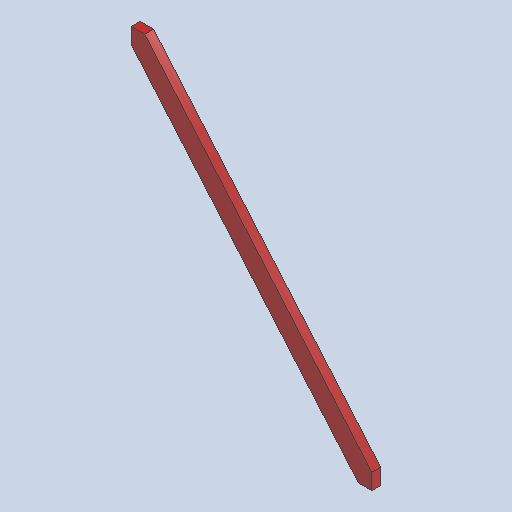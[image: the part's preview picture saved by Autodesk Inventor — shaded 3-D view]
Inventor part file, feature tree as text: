
AUTODESK INVENTOR PART (.ipt)
format: ipt  version: 2025 (Build 290162000, 162)  size: 95,744 bytes
history: native  units: in
note: dims shown in document units (in); Inventor stores cm internally (conversion verified against a paired STEP export)
features: other x4, sketch x1
ambient origin geometry x8: Origin, YZ Plane, XZ Plane, XY Plane, X Axis, Y Axis, Z Axis, Center Point
bodies: Solid1 (feature_tree)
feature tree (5):
  other  "44x2x4_MIR.ipt"
  other  "Solid1::44x2x4_MIR.ipt"
  other  "TaggingFeature1"
  sketch  "Sketch1"  dims[d0=0.3937in]
  other  "Finish1"
